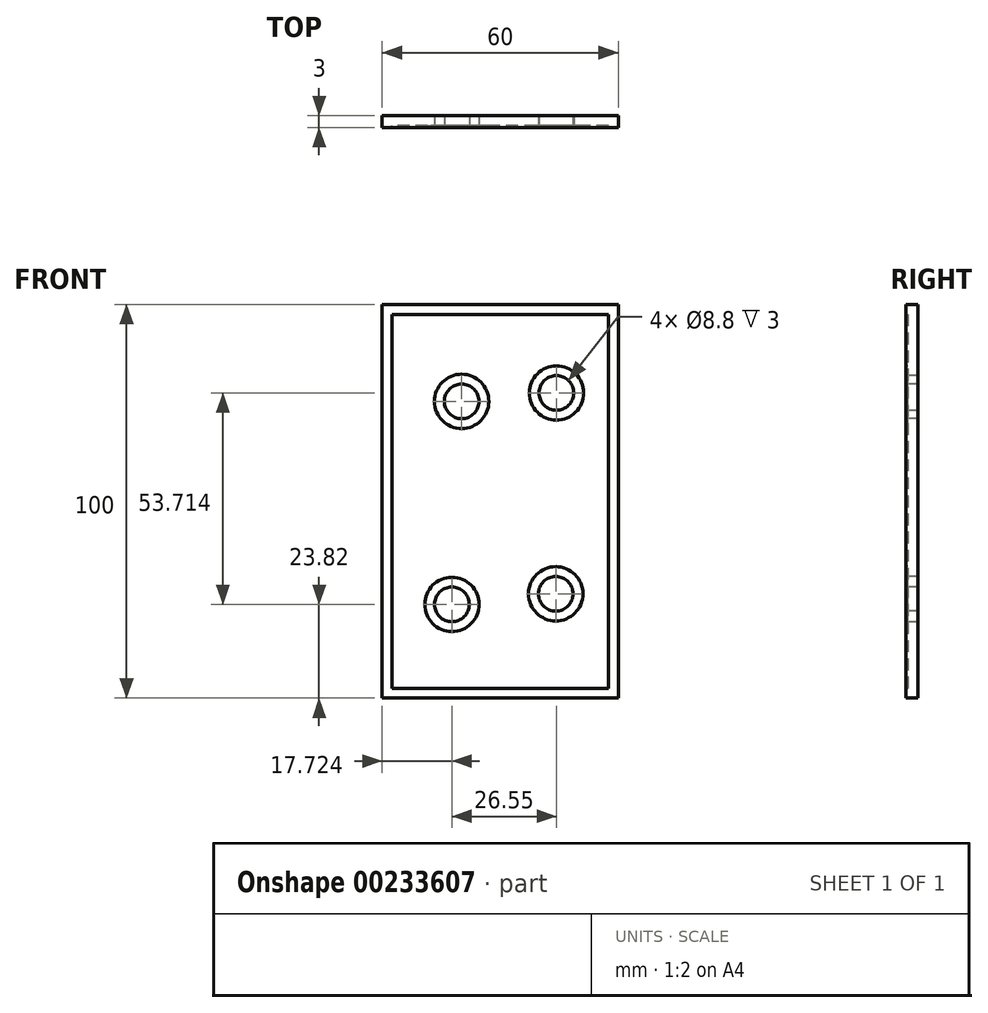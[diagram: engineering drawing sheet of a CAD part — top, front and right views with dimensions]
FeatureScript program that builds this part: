
annotation { "Feature Type Name" : "Feature", "Feature Type Description" : "" }
export const myFeature = defineFeature(function(context is Context, id is Id, definition is map)
    precondition{}
    {
        {
            var Q0;
            Q0=qCreatedBy(makeId("Front.planeOp"),FACE);
            var sketch = newSketch(context, id + "F0", { "sketchPlane" : qUnion([Q0])});
            skLineSegment(sketch, "E0.bottom", {"start": v(30, 50) * mm, "end": v(-30, 50) * mm});
            skLineSegment(sketch, "E0.top", {"start": v(30, -50) * mm, "end": v(-30, -50) * mm});
            skLineSegment(sketch, "E0.left", {"start": v(30, 50) * mm, "end": v(30, -50) * mm});
            skLineSegment(sketch, "E0.right", {"start": v(-30, 50) * mm, "end": v(-30, -50) * mm});
            skPoint(sketch, "E0.middle", {"position": v(0, 0) * mm});
            skSolve(sketch);
        }
        {
            var Q0;
            Q0=makeQuery(id+"F0.imprint","IMPRINT",FACE,{"disambiguationData":[TD([[makeQuery(id+"F0.imprint","IMPRINT",EDGE,{"derivedFrom":sQuery(id+"F0.wireOp",EDGE,"E0.bottom")}),1.0]])]});
            extrude(context, id + "F1", {"entities" : qUnion([Q0]), "depth" : 3 * mm});
        }
        {
            var Q0;
            Q0=makeQuery(id+"F1.opExtrude","CAP_FACE",FACE,{"disambiguationData":[OSD([sQuery(id+"F0.wireOp",EDGE,"E0.bottom"),sQuery(id+"F0.wireOp",EDGE,"E0.top"),sQuery(id+"F0.wireOp",EDGE,"E0.left"),sQuery(id+"F0.wireOp",EDGE,"E0.right")])],"isStart":false});
            var sketch = newSketch(context, id + "F2", { "sketchPlane" : qUnion([Q0])});
            skPoint(sketch, "E1", {"position": v(-12.28, -26.18) * mm});
            skPoint(sketch, "E2", {"position": v(14.1, -23.48) * mm});
            skPoint(sketch, "E3", {"position": v(14.27, 27.53) * mm});
            skPoint(sketch, "E4", {"position": v(-9.8, 25.41) * mm});
            skSolve(sketch);
        }
        {
            var Q0;
            Q0=sQuery(id+"F2.wireOp",VERTEX,"E4");
            var Q1;
            Q1=sQuery(id+"F2.wireOp",VERTEX,"E3");
            var Q2;
            Q2=sQuery(id+"F2.wireOp",VERTEX,"E2");
            var Q3;
            Q3=sQuery(id+"F2.wireOp",VERTEX,"E1");
            var Q4;
            Q4=makeQuery(id+"F1.opExtrude","SWEPT_BODY",BODY,{"disambiguationData":[OSD([sQuery(id+"F0.wireOp",EDGE,"E0.bottom"),sQuery(id+"F0.wireOp",EDGE,"E0.top"),sQuery(id+"F0.wireOp",EDGE,"E0.left"),sQuery(id+"F0.wireOp",EDGE,"E0.right")])]});
            hole(context, id + "F3", {"style" : HoleStyle.SIMPLE, "endStyle" : HoleEndStyle.THROUGH, "standardTappedOrClearance" : lookupTablePath({ "standard" : "ISO", "engagement" : "75%", "pitch" : "1.25 mm", "size" : "M10", "type" : "Tapped" }), "standardBlindInLast" : lookupTablePath({ "standard" : "ISO", "engagement" : "75%", "pitch" : "1.25 mm", "size" : "M10", "type" : "Tapped" }), "holeDiameter" : 8.8 * mm, "locations" : qUnion([Q0, Q1, Q2, Q3]), "scope" : qUnion([Q4]), "isTappedThrough" : true, "majorDiameter" : 10 * mm, "showTappedDepth" : true});
        }
        {
            var Q0;
            Q0=makeQuery(id+"F1.opExtrude","CAP_FACE",FACE,{"disambiguationData":[OSD([sQuery(id+"F0.wireOp",EDGE,"E0.bottom"),sQuery(id+"F0.wireOp",EDGE,"E0.top"),sQuery(id+"F0.wireOp",EDGE,"E0.left"),sQuery(id+"F0.wireOp",EDGE,"E0.right")])],"isStart":false});
            shell(context, id + "F4", {"entities" : qUnion([Q0]), "thickness" : 2.5 * mm});
        }
    });
